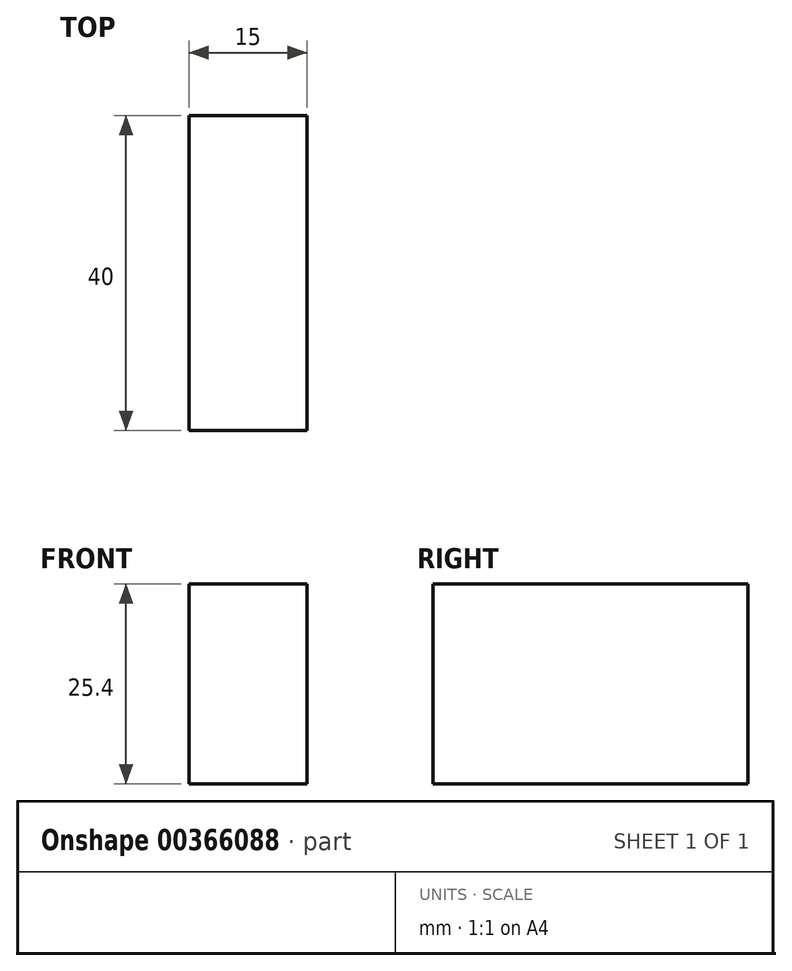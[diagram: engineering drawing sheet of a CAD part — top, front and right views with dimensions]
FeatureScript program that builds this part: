
annotation { "Feature Type Name" : "Feature", "Feature Type Description" : "" }
export const myFeature = defineFeature(function(context is Context, id is Id, definition is map)
    precondition{}
    {
        {
            var Q0;
            Q0=qCreatedBy(makeId("Top.planeOp"),FACE);
            var sketch = newSketch(context, id + "F0", { "sketchPlane" : qUnion([Q0])});
            skLineSegment(sketch, "E0.bottom", {"start": v(-7.5, 20) * mm, "end": v(7.5, 20) * mm});
            skLineSegment(sketch, "E0.top", {"start": v(-7.5, -20) * mm, "end": v(7.5, -20) * mm});
            skLineSegment(sketch, "E0.left", {"start": v(-7.5, 20) * mm, "end": v(-7.5, -20) * mm});
            skLineSegment(sketch, "E0.right", {"start": v(7.5, 20) * mm, "end": v(7.5, -20) * mm});
            skPoint(sketch, "E0.middle", {"position": v(0, 0) * mm});
            skSolve(sketch);
        }
        {
            var Q0;
            Q0 = qSketchRegion(id + "F0", true);
            extrude(context, id + "F1", {"entities" : qUnion([Q0]), "depth" : 25.4 * mm});
        }
    });
